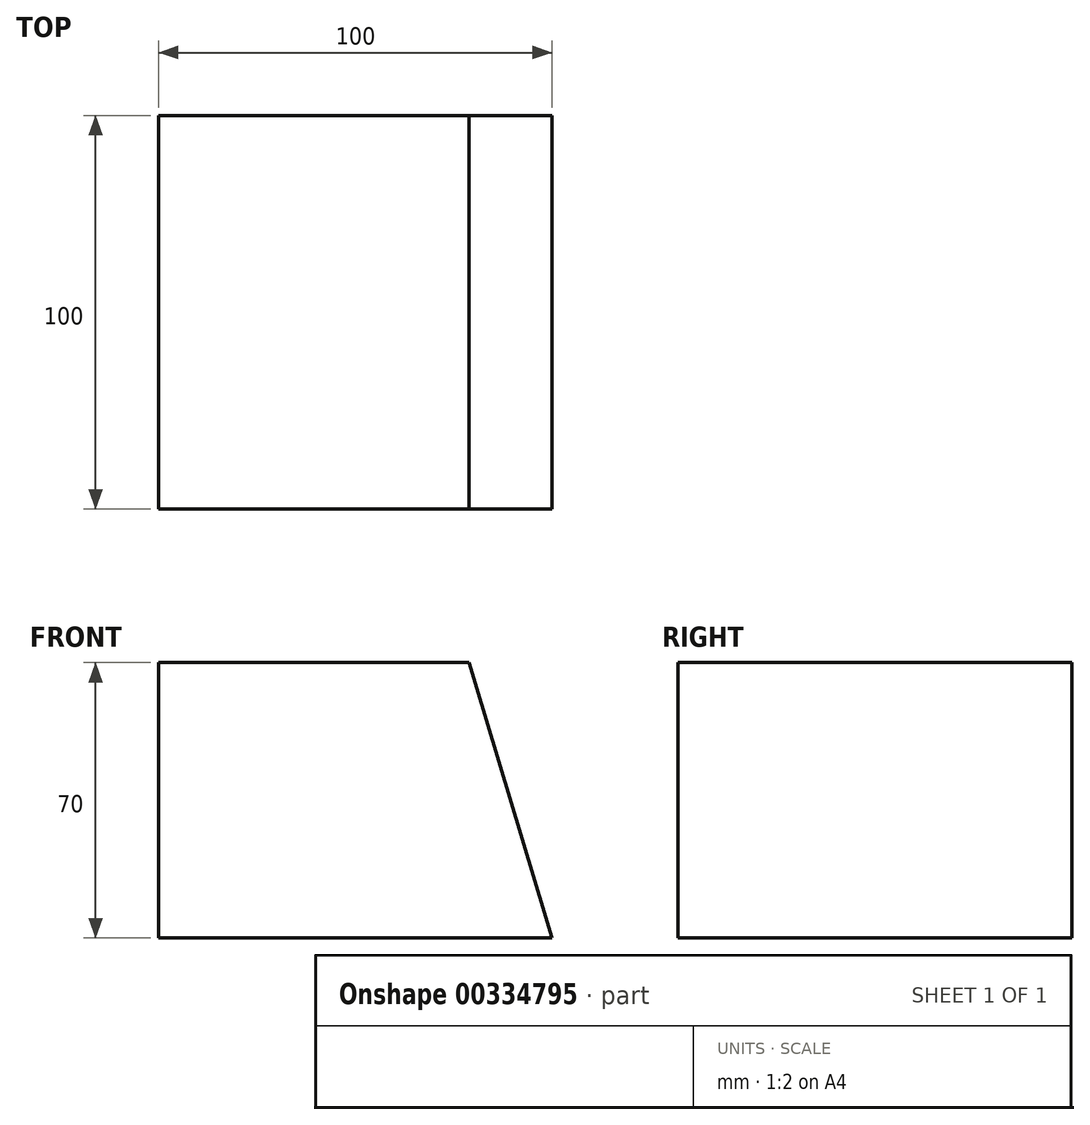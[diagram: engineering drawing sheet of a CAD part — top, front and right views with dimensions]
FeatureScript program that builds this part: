
annotation { "Feature Type Name" : "Feature", "Feature Type Description" : "" }
export const myFeature = defineFeature(function(context is Context, id is Id, definition is map)
    precondition{}
    {
        {
            var Q0;
            Q0=qCreatedBy(makeId("Top.planeOp"),FACE);
            var sketch = newSketch(context, id + "F0", { "sketchPlane" : qUnion([Q0])});
            skLineSegment(sketch, "E0.bottom", {"start": v(50, 50) * mm, "end": v(-50, 50) * mm});
            skLineSegment(sketch, "E0.top", {"start": v(50, -50) * mm, "end": v(-50, -50) * mm});
            skLineSegment(sketch, "E0.left", {"start": v(50, 50) * mm, "end": v(50, -50) * mm});
            skLineSegment(sketch, "E0.right", {"start": v(-50, 50) * mm, "end": v(-50, -50) * mm});
            skPoint(sketch, "E0.middle", {"position": v(0, 0) * mm});
            skSolve(sketch);
        }
        {
            var Q0;
            Q0=qCreatedBy(makeId("Top.planeOp"),FACE);
            cPlane(context, id + "F1", {"entities" : qUnion([Q0]), "cplaneType" : CPlaneType.OFFSET, "offset" : 70 * mm, "width" : 150 * mm, "height" : 150 * mm});
        }
        {
            var Q0;
            Q0=qCreatedBy(id+"F1.planeOp",FACE);
            var sketch = newSketch(context, id + "F2", { "sketchPlane" : qUnion([Q0])});
            skCircle(sketch, "E1.cCircle", {"center": v(0, 0) * mm, "radius": 25 * mm, "construction": true});
            skLineSegment(sketch, "E1.0", {"start": v(-50, 25) * mm, "end": v(14.43, 25) * mm});
            skLineSegment(sketch, "E1.1", {"start": v(0, 50) * mm, "end": v(28.87, 0) * mm});
            skLineSegment(sketch, "E1.3", {"start": v(50, -25) * mm, "end": v(-14.43, -25) * mm});
            skLineSegment(sketch, "E1.4", {"start": v(0, -50) * mm, "end": v(-28.87, 0) * mm});
            skLineSegment(sketch, "E1.5", {"start": v(-50, -36.6) * mm, "end": v(-14.43, 25) * mm});
            skPoint(sketch, "E1.0.midPoint", {"position": v(0, 25) * mm});
            skLineSegment(sketch, "E2.bottom", {"start": v(50, 50) * mm, "end": v(-50, 50) * mm});
            skLineSegment(sketch, "E2.top", {"start": v(50, -50) * mm, "end": v(-50, -50) * mm});
            skLineSegment(sketch, "E2.left", {"start": v(50, 50) * mm, "end": v(50, -50) * mm});
            skLineSegment(sketch, "E2.right", {"start": v(-50, 50) * mm, "end": v(-50, -50) * mm});
            skLineSegment(sketch, "E3", {"start": v(14.43, -25) * mm, "end": v(50, 36.6) * mm});
            skSolve(sketch);
        }
        {
            var Q0;
            Q0=makeQuery(id+"F0.imprint","IMPRINT",FACE,{"disambiguationData":[TD([[makeQuery(id+"F0.imprint","IMPRINT",EDGE,{"derivedFrom":sQuery(id+"F0.wireOp",EDGE,"E0.bottom")}),1.0]])]});
            extrude(context, id + "F3", {"entities" : qUnion([Q0]), "depth" : 70 * mm});
        }
        {
            var Q0;
            Q0=makeQuery(id+"F3.opExtrude","SWEPT_FACE",FACE,{"disambiguationData":[OSD([sQuery(id+"F0.wireOp",EDGE,"E0.top")])]});
            var sketch = newSketch(context, id + "F4", { "sketchPlane" : qUnion([Q0])});
            skLineSegment(sketch, "E4", {"start": v(28.87, 70) * mm, "end": v(50, 0) * mm});
            skLineSegment(sketch, "E5", {"start": v(-50, 70) * mm, "end": v(-50, 0) * mm});
            skSolve(sketch);
        }
        {
            var Q0;
            Q0 = qSketchRegion(id + "F4", true);
            var Q1;
            {var subQ0=sQuery(id+"F4.wireOp",EDGE,"E5");Q1=makeQuery(id+"F4.imprint","IMPRINT",FACE,{"disambiguationData":[TD([[makeQuery(id+"F4.imprint","IMPRINT",EDGE,{"derivedFrom":subQ0}),-1.0]])]});}
            var Q2;
            {var subQ0=sQuery(id+"F4.wireOp",EDGE,"E4");Q2=makeQuery(id+"F4.imprint","IMPRINT",FACE,{"disambiguationData":[TD([[makeQuery(id+"F4.imprint","IMPRINT",EDGE,{"derivedFrom":subQ0}),1.0]])]});}
            extrude(context, id + "F5", {"entities" : qUnion([Q0, Q1, Q2]), "operationType" : NewBodyOperationType.REMOVE, "oppositeDirection" : true, "depth" : 100 * mm});
        }
    });
